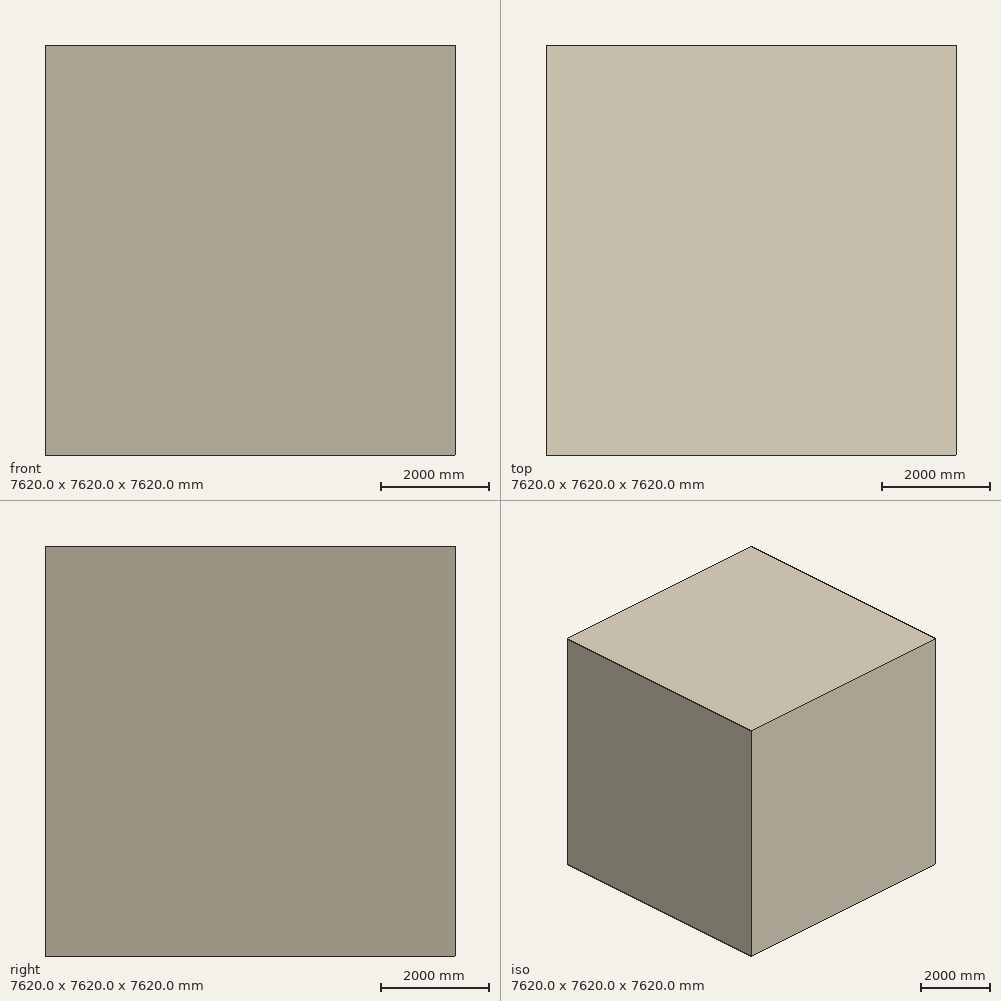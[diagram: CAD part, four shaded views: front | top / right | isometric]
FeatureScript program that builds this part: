
annotation { "Feature Type Name" : "Feature", "Feature Type Description" : "" }
export const myFeature = defineFeature(function(context is Context, id is Id, definition is map)
    precondition{}
    {
        {
            var Q0;
            Q0=qCreatedBy(makeId("Top.planeOp"),FACE);
            var sketch = newSketch(context, id + "F0", { "sketchPlane" : qUnion([Q0])});
            skLineSegment(sketch, "E0.bottom", {"start": v(-3808.65, 4801.66) * mm, "end": v(3811.35, 4801.66) * mm});
            skLineSegment(sketch, "E0.top", {"start": v(-3808.65, -2818.34) * mm, "end": v(3811.35, -2818.34) * mm});
            skLineSegment(sketch, "E0.left", {"start": v(-3808.65, 4801.66) * mm, "end": v(-3808.65, -2818.34) * mm});
            skLineSegment(sketch, "E0.right", {"start": v(3811.35, 4801.66) * mm, "end": v(3811.35, -2818.34) * mm});
            skSolve(sketch);
        }
        {
            var Q0;
            Q0 = qSketchRegion(id + "F0", true);
            extrude(context, id + "F1", {"entities" : qUnion([Q0]), "endBound" : BoundingType.SYMMETRIC, "oppositeDirection" : true, "depth" : 7620 * mm, "offsetDistance" : 25.4 * mm});
        }
    });
